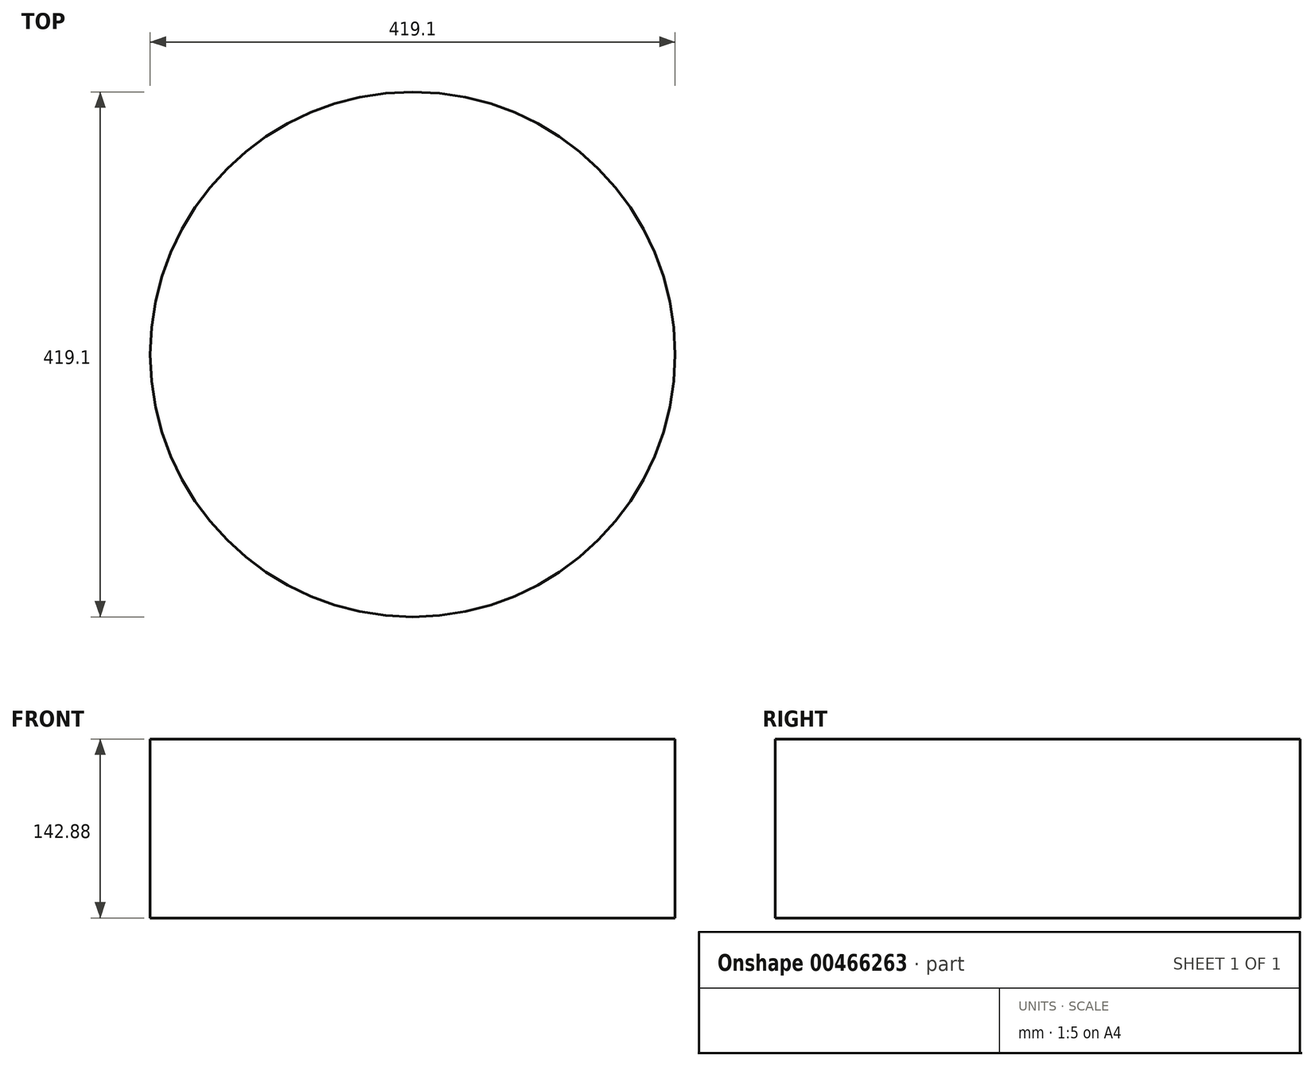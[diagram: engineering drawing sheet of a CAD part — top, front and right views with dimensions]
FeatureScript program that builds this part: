
annotation { "Feature Type Name" : "Feature", "Feature Type Description" : "" }
export const myFeature = defineFeature(function(context is Context, id is Id, definition is map)
    precondition{}
    {
        {
            var Q0;
            Q0=qCreatedBy(makeId("Top.planeOp"),FACE);
            var sketch = newSketch(context, id + "F0", { "sketchPlane" : qUnion([Q0])});
            skCircle(sketch, "E0", {"center": v(0, 0) * mm, "radius": 209.55 * mm});
            skSolve(sketch);
        }
        {
            var Q0;
            Q0 = qSketchRegion(id + "F0", true);
            extrude(context, id + "F1", {"entities" : qUnion([Q0]), "depth" : 142.88 * mm});
        }
    });
